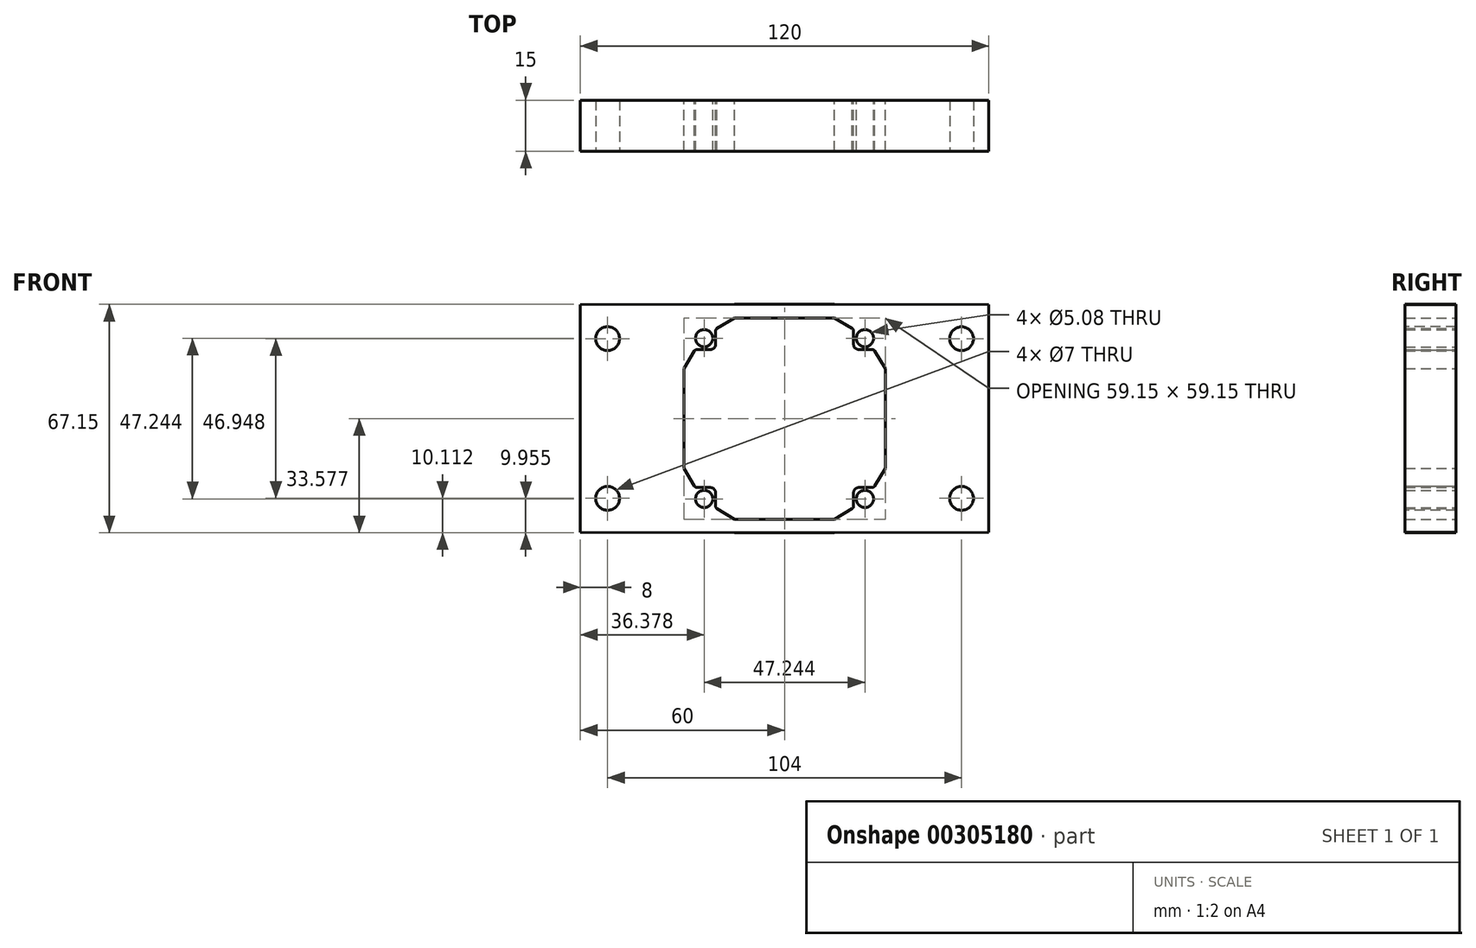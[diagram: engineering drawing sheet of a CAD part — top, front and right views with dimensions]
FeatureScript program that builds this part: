
annotation { "Feature Type Name" : "Feature", "Feature Type Description" : "" }
export const myFeature = defineFeature(function(context is Context, id is Id, definition is map)
    precondition{}
    {
        {
            var Q0;
            Q0=qCreatedBy(makeId("Front.planeOp"),FACE);
            var sketch = newSketch(context, id + "F0", { "sketchPlane" : qUnion([Q0])});
            skCircle(sketch, "E0.0", {"center": v(23.32, 23.03) * mm, "radius": 2.54 * mm});
            skCircle(sketch, "E1.0", {"center": v(-23.92, -24.22) * mm, "radius": 2.54 * mm});
            skCircle(sketch, "E2.0", {"center": v(23.32, -24.22) * mm, "radius": 2.54 * mm});
            skLineSegment(sketch, "E3.0", {"start": v(-20.58, 25.11) * mm, "end": v(-20.58, 21.23) * mm});
            skLineSegment(sketch, "E4.0", {"start": v(-22.12, 19.69) * mm, "end": v(-26, 19.69) * mm});
            skLineSegment(sketch, "E5.0", {"start": v(-26, -20.87) * mm, "end": v(-22.12, -20.87) * mm});
            skLineSegment(sketch, "E6.0", {"start": v(-20.58, -22.41) * mm, "end": v(-20.58, -26.3) * mm});
            skArc(sketch, "E7", {"start": v(-26, -20.87) * mm, "mid": v(-26.45, -20.77) * mm, "end": v(-26.8, -20.47) * mm});
            skArc(sketch, "E8", {"start": v(-20.58, -26.3) * mm, "mid": v(-20.47, -26.75) * mm, "end": v(-20.18, -27.1) * mm});
            skArc(sketch, "E9", {"start": v(-26.8, 19.29) * mm, "mid": v(-26.45, 19.58) * mm, "end": v(-26, 19.69) * mm});
            skArc(sketch, "E10", {"start": v(-22.12, 19.69) * mm, "mid": v(-21.03, 20.14) * mm, "end": v(-20.58, 21.23) * mm});
            skArc(sketch, "E11", {"start": v(-20.58, 25.11) * mm, "mid": v(-20.47, 25.56) * mm, "end": v(-20.18, 25.91) * mm});
            skArc(sketch, "E12.MirrorCS", {"start": v(19.98, 25.11) * mm, "mid": v(19.87, 25.56) * mm, "end": v(19.58, 25.91) * mm});
            skLineSegment(sketch, "E13.MirrorCS", {"start": v(19.98, 25.11) * mm, "end": v(19.98, 21.23) * mm});
            skArc(sketch, "E14.MirrorCS", {"start": v(21.52, 19.69) * mm, "mid": v(20.43, 20.14) * mm, "end": v(19.98, 21.23) * mm});
            skLineSegment(sketch, "E15.MirrorCS", {"start": v(21.52, 19.69) * mm, "end": v(25.4, 19.69) * mm});
            skArc(sketch, "E16.MirrorCS", {"start": v(26.2, 19.29) * mm, "mid": v(25.85, 19.58) * mm, "end": v(25.4, 19.69) * mm});
            skLineSegment(sketch, "E17.MirrorCS", {"start": v(25.4, -20.87) * mm, "end": v(21.52, -20.87) * mm});
            skArc(sketch, "E18.MirrorCS", {"start": v(25.4, -20.87) * mm, "mid": v(25.85, -20.77) * mm, "end": v(26.2, -20.47) * mm});
            skArc(sketch, "E19.MirrorCS", {"start": v(21.52, -20.87) * mm, "mid": v(20.43, -21.32) * mm, "end": v(19.98, -22.41) * mm});
            skLineSegment(sketch, "E20.MirrorCS", {"start": v(19.98, -22.41) * mm, "end": v(19.98, -26.3) * mm});
            skArc(sketch, "E21.MirrorCS", {"start": v(19.98, -26.3) * mm, "mid": v(19.87, -26.75) * mm, "end": v(19.58, -27.1) * mm});
            skCircle(sketch, "E22.0", {"center": v(-23.92, 23.03) * mm, "radius": 2.54 * mm});
            skLineSegment(sketch, "E23", {"start": v(-60.3, -34.06) * mm, "end": v(-60.3, 32.87) * mm});
            skLineSegment(sketch, "E24.MirrorCS", {"start": v(59.7, -34.06) * mm, "end": v(59.7, 32.87) * mm});
            skLineSegment(sketch, "E25.0", {"start": v(-15, 28.98) * mm, "end": v(14.4, 28.98) * mm});
            skLineSegment(sketch, "E26.0", {"start": v(14.4, -30.17) * mm, "end": v(-15, -30.17) * mm});
            skLineSegment(sketch, "E27", {"start": v(-20.18, 25.91) * mm, "end": v(-15, 28.98) * mm});
            skLineSegment(sketch, "E28", {"start": v(14.4, 27.98) * mm, "end": v(14.4, 28.98) * mm, "construction": true});
            skLineSegment(sketch, "E29", {"start": v(14.4, 28.98) * mm, "end": v(19.58, 25.91) * mm});
            skLineSegment(sketch, "E30", {"start": v(-20.18, -27.1) * mm, "end": v(-15, -30.17) * mm});
            skLineSegment(sketch, "E31", {"start": v(14.4, -30.17) * mm, "end": v(19.58, -27.1) * mm});
            skLineSegment(sketch, "E32", {"start": v(-28.87, -15.29) * mm, "end": v(-29.87, -15.29) * mm});
            skLineSegment(sketch, "E33", {"start": v(-26.8, -20.47) * mm, "end": v(-29.87, -15.29) * mm});
            skLineSegment(sketch, "E34", {"start": v(-28.87, 14.1) * mm, "end": v(-29.87, 14.1) * mm});
            skLineSegment(sketch, "E35", {"start": v(-29.87, 14.1) * mm, "end": v(-29.87, -15.29) * mm});
            skLineSegment(sketch, "E36", {"start": v(-29.87, 14.1) * mm, "end": v(-26.8, 19.29) * mm});
            skLineSegment(sketch, "E37", {"start": v(28.28, 14.1) * mm, "end": v(29.28, 14.1) * mm});
            skLineSegment(sketch, "E38", {"start": v(28.28, -15.29) * mm, "end": v(29.28, -15.29) * mm});
            skLineSegment(sketch, "E39", {"start": v(29.28, -15.29) * mm, "end": v(29.28, 14.1) * mm});
            skLineSegment(sketch, "E40", {"start": v(26.2, 19.29) * mm, "end": v(29.28, 14.1) * mm});
            skLineSegment(sketch, "E41", {"start": v(26.2, -20.47) * mm, "end": v(29.28, -15.29) * mm});
            skArc(sketch, "E42", {"start": v(-22.12, -20.87) * mm, "mid": v(-21.03, -21.32) * mm, "end": v(-20.58, -22.41) * mm});
            skLineSegment(sketch, "E43.0", {"start": v(-15, 32.98) * mm, "end": v(14.4, 32.98) * mm});
            skLineSegment(sketch, "E44.0", {"start": v(14.4, -34.17) * mm, "end": v(-15, -34.17) * mm});
            skLineSegment(sketch, "E45", {"start": v(-60.3, -34.06) * mm, "end": v(-15, -34.17) * mm});
            skLineSegment(sketch, "E46", {"start": v(14.4, -34.17) * mm, "end": v(59.7, -34.06) * mm});
            skLineSegment(sketch, "E47", {"start": v(-15, 32.98) * mm, "end": v(-60.3, 32.87) * mm});
            skLineSegment(sketch, "E48", {"start": v(14.4, 32.98) * mm, "end": v(59.7, 32.87) * mm});
            skSolve(sketch);
        }
        {
            var Q0;
            Q0=makeQuery(id+"F0.imprint","IMPRINT",FACE,{"disambiguationData":[TD([[makeQuery(id+"F0.imprint","IMPRINT",EDGE,{"derivedFrom":sQuery(id+"F0.wireOp",EDGE,"E0.0")}),-1.0]])]});
            extrude(context, id + "F1", {"entities" : qUnion([Q0]), "depth" : 15 * mm, "offsetDistance" : 25 * mm});
        }
        {
            var Q0;
            Q0=makeQuery(id+"F1.opExtrude","CAP_FACE",FACE,{"disambiguationData":[OSD([sQuery(id+"F0.wireOp",EDGE,"E0.0"),sQuery(id+"F0.wireOp",EDGE,"E1.0"),sQuery(id+"F0.wireOp",EDGE,"E2.0"),sQuery(id+"F0.wireOp",EDGE,"E3.0"),sQuery(id+"F0.wireOp",EDGE,"E4.0"),sQuery(id+"F0.wireOp",EDGE,"E5.0"),sQuery(id+"F0.wireOp",EDGE,"E6.0"),sQuery(id+"F0.wireOp",EDGE,"E7"),sQuery(id+"F0.wireOp",EDGE,"E8"),sQuery(id+"F0.wireOp",EDGE,"E9"),sQuery(id+"F0.wireOp",EDGE,"E10"),sQuery(id+"F0.wireOp",EDGE,"E11"),sQuery(id+"F0.wireOp",EDGE,"E12.MirrorCS"),sQuery(id+"F0.wireOp",EDGE,"E13.MirrorCS"),sQuery(id+"F0.wireOp",EDGE,"E14.MirrorCS"),sQuery(id+"F0.wireOp",EDGE,"E15.MirrorCS"),sQuery(id+"F0.wireOp",EDGE,"E16.MirrorCS"),sQuery(id+"F0.wireOp",EDGE,"E17.MirrorCS"),sQuery(id+"F0.wireOp",EDGE,"E18.MirrorCS"),sQuery(id+"F0.wireOp",EDGE,"E19.MirrorCS"),sQuery(id+"F0.wireOp",EDGE,"E20.MirrorCS"),sQuery(id+"F0.wireOp",EDGE,"E21.MirrorCS"),sQuery(id+"F0.wireOp",EDGE,"E22.0"),sQuery(id+"F0.wireOp",EDGE,"E23"),sQuery(id+"F0.wireOp",EDGE,"E24.MirrorCS"),sQuery(id+"F0.wireOp",EDGE,"E25.0"),sQuery(id+"F0.wireOp",EDGE,"E26.0"),sQuery(id+"F0.wireOp",EDGE,"E27"),sQuery(id+"F0.wireOp",EDGE,"E29"),sQuery(id+"F0.wireOp",EDGE,"E30"),sQuery(id+"F0.wireOp",EDGE,"E31"),sQuery(id+"F0.wireOp",EDGE,"E33"),sQuery(id+"F0.wireOp",EDGE,"E35"),sQuery(id+"F0.wireOp",EDGE,"E36"),sQuery(id+"F0.wireOp",EDGE,"E39"),sQuery(id+"F0.wireOp",EDGE,"E40"),sQuery(id+"F0.wireOp",EDGE,"E41"),sQuery(id+"F0.wireOp",EDGE,"E42"),sQuery(id+"F0.wireOp",EDGE,"E43.0"),sQuery(id+"F0.wireOp",EDGE,"E44.0"),sQuery(id+"F0.wireOp",EDGE,"E45"),sQuery(id+"F0.wireOp",EDGE,"E46"),sQuery(id+"F0.wireOp",EDGE,"E47"),sQuery(id+"F0.wireOp",EDGE,"E48")])],"isStart":false});
            var sketch = newSketch(context, id + "F2", { "sketchPlane" : qUnion([Q0])});
            skCircle(sketch, "E49", {"center": v(-52.3, 22.9) * mm, "radius": 3.5 * mm});
            skPoint(sketch, "E49.centerSnap0", {"position": v(-20.58, 22.9) * mm});
            skCircle(sketch, "E50", {"center": v(51.7, 22.87) * mm, "radius": 3.5 * mm});
            skCircle(sketch, "E51", {"center": v(-52.3, -24.06) * mm, "radius": 3.5 * mm});
            skCircle(sketch, "E52", {"center": v(51.7, -24.06) * mm, "radius": 3.5 * mm});
            skCircle(sketch, "E53", {"center": v(-42.3, 22.9) * mm, "radius": 3.5 * mm});
            skCircle(sketch, "E54", {"center": v(-42.3, -24.06) * mm, "radius": 3.5 * mm});
            skCircle(sketch, "E55", {"center": v(41.7, 22.87) * mm, "radius": 3.5 * mm});
            skCircle(sketch, "E56", {"center": v(41.7, -24.06) * mm, "radius": 3.5 * mm});
            skLineSegment(sketch, "E57", {"start": v(51.7, 26.37) * mm, "end": v(41.7, 26.37) * mm});
            skLineSegment(sketch, "E58", {"start": v(51.7, 19.37) * mm, "end": v(41.7, 19.37) * mm});
            skLineSegment(sketch, "E59.MirrorCS", {"start": v(-51.7, 26.37) * mm, "end": v(-41.7, 26.37) * mm});
            skLineSegment(sketch, "E60.MirrorCS", {"start": v(-51.7, 19.37) * mm, "end": v(-41.7, 19.37) * mm});
            skSolve(sketch);
        }
        {
            var Q0;
            Q0=makeQuery(id+"F2.imprint","IMPRINT",FACE,{"disambiguationData":[TD([[makeQuery(id+"F2.imprint","IMPRINT",EDGE,{"derivedFrom":sQuery(id+"F2.wireOp",EDGE,"E49")}),1.0]])]});
            var Q1;
            Q1=makeQuery(id+"F2.imprint","IMPRINT",FACE,{"disambiguationData":[TD([[makeQuery(id+"F2.imprint","IMPRINT",EDGE,{"derivedFrom":sQuery(id+"F2.wireOp",EDGE,"E51")}),1.0]])]});
            var Q2;
            Q2=makeQuery(id+"F2.imprint","IMPRINT",FACE,{"disambiguationData":[TD([[makeQuery(id+"F2.imprint","IMPRINT",EDGE,{"derivedFrom":sQuery(id+"F2.wireOp",EDGE,"E50")}),1.0]])]});
            var Q3;
            Q3=makeQuery(id+"F2.imprint","IMPRINT",FACE,{"disambiguationData":[TD([[makeQuery(id+"F2.imprint","IMPRINT",EDGE,{"derivedFrom":sQuery(id+"F2.wireOp",EDGE,"E52")}),1.0]])]});
            extrude(context, id + "F3", {"entities" : qUnion([Q0, Q1, Q2, Q3]), "operationType" : NewBodyOperationType.REMOVE, "oppositeDirection" : true, "depth" : 25 * mm, "offsetDistance" : 25 * mm});
        }
    });
